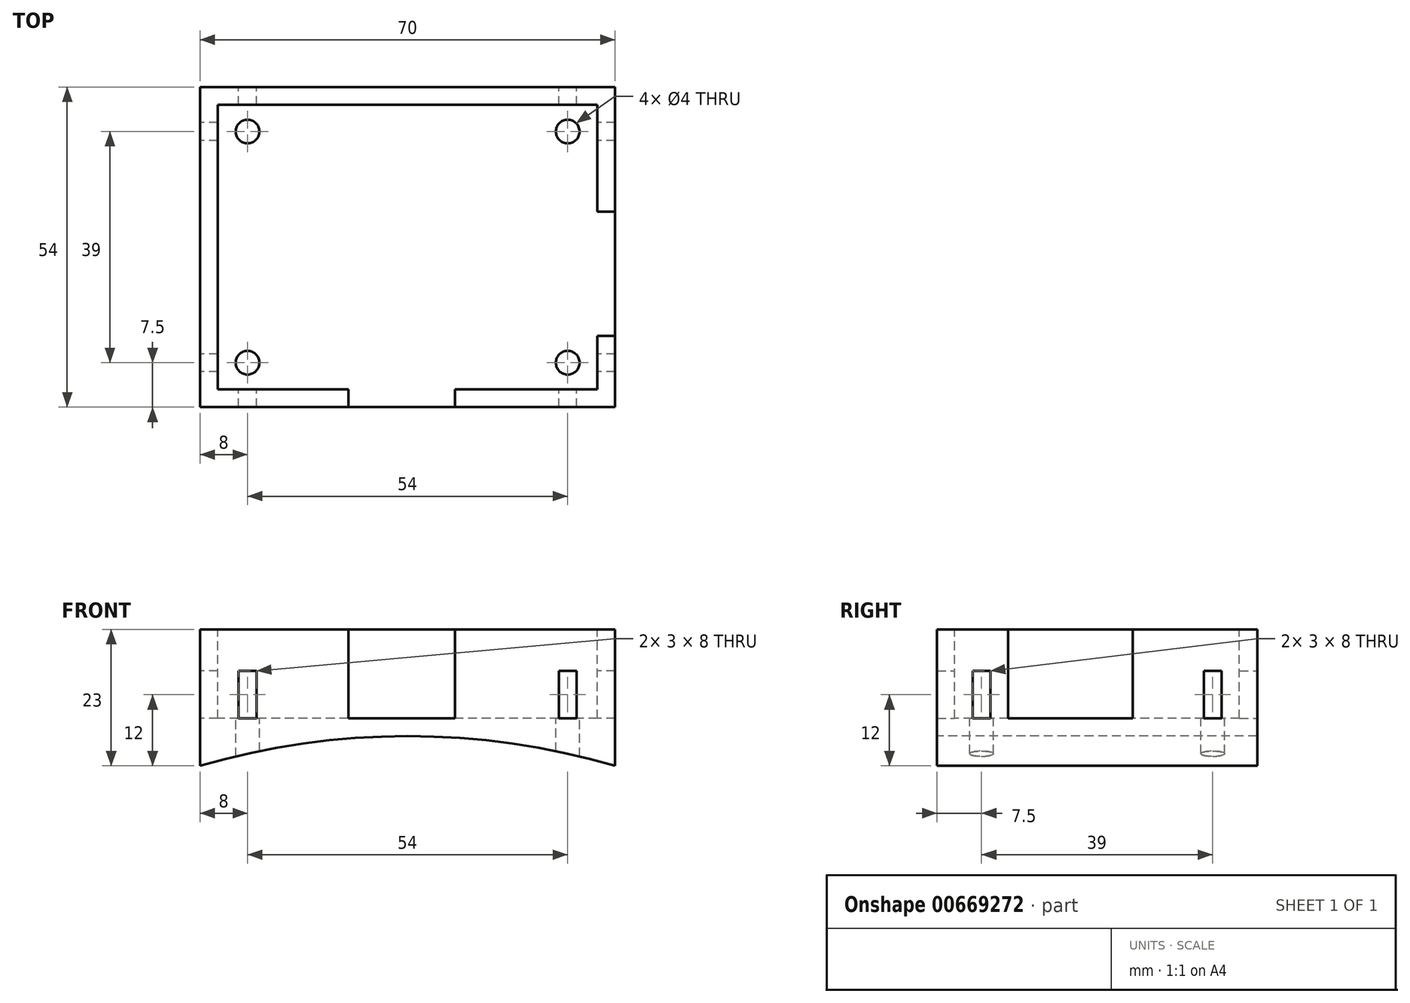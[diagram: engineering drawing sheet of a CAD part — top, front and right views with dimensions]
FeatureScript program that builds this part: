
annotation { "Feature Type Name" : "Feature", "Feature Type Description" : "" }
export const myFeature = defineFeature(function(context is Context, id is Id, definition is map)
    precondition{}
    {
        {
            var Q0;
            Q0=qCreatedBy(makeId("Top.planeOp"),FACE);
            var sketch = newSketch(context, id + "F0", { "sketchPlane" : qUnion([Q0])});
            skLineSegment(sketch, "E0.bottom", {"start": v(35, -27) * mm, "end": v(-35, -27) * mm});
            skLineSegment(sketch, "E0.top", {"start": v(35, 27) * mm, "end": v(-35, 27) * mm});
            skLineSegment(sketch, "E0.left", {"start": v(35, -27) * mm, "end": v(35, 27) * mm});
            skLineSegment(sketch, "E0.right", {"start": v(-35, -27) * mm, "end": v(-35, 27) * mm});
            skPoint(sketch, "E0.middle", {"position": v(0, 0) * mm});
            skSolve(sketch);
        }
        {
            var Q0;
            Q0=makeQuery(id+"F0.imprint","IMPRINT",FACE,{"disambiguationData":[TD([[makeQuery(id+"F0.imprint","IMPRINT",EDGE,{"derivedFrom":sQuery(id+"F0.wireOp",EDGE,"E0.bottom")}),-1.0]])]});
            extrude(context, id + "F1", {"entities" : qUnion([Q0]), "oppositeDirection" : true, "depth" : 23 * mm, "offsetDistance" : 25 * mm});
        }
        {
            var Q0;
            Q0=makeQuery(id+"F1.opExtrude","SWEPT_FACE",FACE,{"disambiguationData":[OSD([sQuery(id+"F0.wireOp",EDGE,"E0.bottom")])]});
            var sketch = newSketch(context, id + "F2", { "sketchPlane" : qUnion([Q0])});
            skArc(sketch, "E1", {"start": v(35, -23) * mm, "mid": v(0, -18) * mm, "end": v(-35, -23) * mm});
            skSolve(sketch);
        }
        {
            var Q0;
            Q0=makeQuery(id+"F2.imprint","IMPRINT",FACE,{"disambiguationData":[TD([[makeQuery(id+"F2.imprint","IMPRINT",EDGE,{"derivedFrom":sQuery(id+"F2.wireOp",EDGE,"E1")}),1.0]])]});
            extrude(context, id + "F3", {"entities" : qUnion([Q0]), "operationType" : NewBodyOperationType.REMOVE, "oppositeDirection" : true, "depth" : 60 * mm, "offsetDistance" : 25 * mm});
        }
        {
            var Q0;
            Q0=makeQuery(id+"F1.opExtrude","CAP_FACE",FACE,{"disambiguationData":[OSD([sQuery(id+"F0.wireOp",EDGE,"E0.bottom"),sQuery(id+"F0.wireOp",EDGE,"E0.top"),sQuery(id+"F0.wireOp",EDGE,"E0.left"),sQuery(id+"F0.wireOp",EDGE,"E0.right")])],"isStart":true});
            var sketch = newSketch(context, id + "F4", { "sketchPlane" : qUnion([Q0])});
            skLineSegment(sketch, "E2.bottom", {"start": v(32, 24) * mm, "end": v(-32, 24) * mm});
            skLineSegment(sketch, "E2.top", {"start": v(32, -24) * mm, "end": v(-32, -24) * mm});
            skLineSegment(sketch, "E2.left", {"start": v(32, 24) * mm, "end": v(32, -24) * mm});
            skLineSegment(sketch, "E2.right", {"start": v(-32, 24) * mm, "end": v(-32, -24) * mm});
            skPoint(sketch, "E2.middle", {"position": v(0, 0) * mm});
            skSolve(sketch);
        }
        {
            var Q0;
            Q0=makeQuery(id+"F4.imprint","IMPRINT",FACE,{"disambiguationData":[TD([[makeQuery(id+"F4.imprint","IMPRINT",EDGE,{"derivedFrom":sQuery(id+"F4.wireOp",EDGE,"E2.bottom")}),1.0]])]});
            extrude(context, id + "F5", {"entities" : qUnion([Q0]), "operationType" : NewBodyOperationType.REMOVE, "oppositeDirection" : true, "depth" : 15 * mm, "offsetDistance" : 25 * mm});
        }
        {
            var Q0;
            Q0=makeQuery(id+"F5.boolean.opBoolean","COPY",FACE,{"derivedFrom":makeQuery(id+"F5.opExtrude","CAP_FACE",FACE,{"disambiguationData":[OSD([sQuery(id+"F4.wireOp",EDGE,"E2.bottom"),sQuery(id+"F4.wireOp",EDGE,"E2.top"),sQuery(id+"F4.wireOp",EDGE,"E2.left"),sQuery(id+"F4.wireOp",EDGE,"E2.right")])],"isStart":false})});
            var sketch = newSketch(context, id + "F6", { "sketchPlane" : qUnion([Q0])});
            skPoint(sketch, "E3.middle", {"position": v(0, 0) * mm});
            skCircle(sketch, "E4", {"center": v(-27, 19.5) * mm, "radius": 2 * mm});
            skCircle(sketch, "E5", {"center": v(-27, -19.5) * mm, "radius": 2 * mm});
            skCircle(sketch, "E6", {"center": v(27, -19.5) * mm, "radius": 2 * mm});
            skCircle(sketch, "E7", {"center": v(27, 19.5) * mm, "radius": 2 * mm});
            skSolve(sketch);
        }
        {
            var Q0;
            Q0 = qSketchRegion(id + "F6", true);
            extrude(context, id + "F7", {"entities" : qUnion([Q0]), "operationType" : NewBodyOperationType.REMOVE, "oppositeDirection" : true, "depth" : 25 * mm, "offsetDistance" : 25 * mm});
        }
        {
            var Q0;
            Q0=makeQuery(id+"F5.boolean.opBoolean","COPY",FACE,{"derivedFrom":makeQuery(id+"F5.opExtrude","CAP_FACE",FACE,{"disambiguationData":[OSD([sQuery(id+"F4.wireOp",EDGE,"E2.bottom"),sQuery(id+"F4.wireOp",EDGE,"E2.top"),sQuery(id+"F4.wireOp",EDGE,"E2.left"),sQuery(id+"F4.wireOp",EDGE,"E2.right")])],"isStart":false})});
            var sketch = newSketch(context, id + "F8", { "sketchPlane" : qUnion([Q0])});
            skLineSegment(sketch, "E8.top", {"start": v(32, 6) * mm, "end": v(37, 6) * mm});
            skLineSegment(sketch, "E9.top", {"start": v(32, -15) * mm, "end": v(38.88, -15) * mm});
            skLineSegment(sketch, "E10.bottom", {"start": v(32, 6) * mm, "end": v(32, 6) * mm});
            skLineSegment(sketch, "E10.top", {"start": v(32, -15) * mm, "end": v(32, -15) * mm});
            skLineSegment(sketch, "E10.left", {"start": v(32, 6) * mm, "end": v(32, -15) * mm});
            skLineSegment(sketch, "E10.right", {"start": v(32, 6) * mm, "end": v(32, -15) * mm});
            skLineSegment(sketch, "E11.bottom", {"start": v(32, 6) * mm, "end": v(38.88, 6) * mm});
            skLineSegment(sketch, "E11.right", {"start": v(38.88, 6) * mm, "end": v(38.88, -15) * mm});
            skSolve(sketch);
        }
        {
            var Q0;
            Q0 = qSketchRegion(id + "F8", true);
            extrude(context, id + "F9", {"entities" : qUnion([Q0]), "operationType" : NewBodyOperationType.REMOVE, "depth" : 25 * mm, "offsetDistance" : 25 * mm});
        }
        {
            var Q0;
            Q0=makeQuery(id+"F9.boolean.opBoolean","MERGE",FACE,{"derivedFrom":[makeQuery(id+"F5.boolean.opBoolean","COPY",FACE,{"derivedFrom":makeQuery(id+"F5.opExtrude","CAP_FACE",FACE,{"disambiguationData":[OSD([sQuery(id+"F4.wireOp",EDGE,"E2.bottom"),sQuery(id+"F4.wireOp",EDGE,"E2.top"),sQuery(id+"F4.wireOp",EDGE,"E2.left"),sQuery(id+"F4.wireOp",EDGE,"E2.right")])],"isStart":false})}),makeQuery(id+"F9.opExtrude","CAP_FACE",FACE,{"disambiguationData":[OSD([sQuery(id+"F8.wireOp",EDGE,"E11.bottom"),sQuery(id+"F8.wireOp",EDGE,"E9.top"),sQuery(id+"F8.wireOp",EDGE,"E10.left"),sQuery(id+"F8.wireOp",EDGE,"E11.right")])],"isStart":true})]});
            var sketch = newSketch(context, id + "F10", { "sketchPlane" : qUnion([Q0])});
            skLineSegment(sketch, "E12.right", {"start": v(-10, -24) * mm, "end": v(-10, -27.84) * mm});
            skLineSegment(sketch, "E13.bottom", {"start": v(8, -24) * mm, "end": v(-10, -24) * mm});
            skLineSegment(sketch, "E13.top", {"start": v(8, -32.82) * mm, "end": v(-10, -32.82) * mm});
            skLineSegment(sketch, "E13.left", {"start": v(8, -24) * mm, "end": v(8, -32.82) * mm});
            skLineSegment(sketch, "E13.right", {"start": v(-10, -24) * mm, "end": v(-10, -32.82) * mm});
            skSolve(sketch);
        }
        {
            var Q0;
            Q0 = qSketchRegion(id + "F10", true);
            extrude(context, id + "F11", {"entities" : qUnion([Q0]), "operationType" : NewBodyOperationType.REMOVE, "depth" : 25 * mm, "offsetDistance" : 25 * mm});
        }
        {
            var Q0;
            Q0=makeQuery(id+"F11.boolean.opBoolean","MERGE",FACE,{"derivedFrom":[makeQuery(id+"F9.boolean.opBoolean","MERGE",FACE,{"derivedFrom":[makeQuery(id+"F5.boolean.opBoolean","COPY",FACE,{"derivedFrom":makeQuery(id+"F5.opExtrude","CAP_FACE",FACE,{"disambiguationData":[OSD([sQuery(id+"F4.wireOp",EDGE,"E2.bottom"),sQuery(id+"F4.wireOp",EDGE,"E2.top"),sQuery(id+"F4.wireOp",EDGE,"E2.left"),sQuery(id+"F4.wireOp",EDGE,"E2.right")])],"isStart":false})}),makeQuery(id+"F9.opExtrude","CAP_FACE",FACE,{"disambiguationData":[OSD([sQuery(id+"F8.wireOp",EDGE,"E11.bottom"),sQuery(id+"F8.wireOp",EDGE,"E9.top"),sQuery(id+"F8.wireOp",EDGE,"E10.left"),sQuery(id+"F8.wireOp",EDGE,"E11.right")])],"isStart":true})]}),makeQuery(id+"F11.opExtrude","CAP_FACE",FACE,{"disambiguationData":[OSD([sQuery(id+"F10.wireOp",EDGE,"E13.bottom"),sQuery(id+"F10.wireOp",EDGE,"E13.top"),sQuery(id+"F10.wireOp",EDGE,"E13.left"),sQuery(id+"F10.wireOp",EDGE,"E13.right")])],"isStart":true})]});
            var sketch = newSketch(context, id + "F12", { "sketchPlane" : qUnion([Q0])});
            skLineSegment(sketch, "E14", {"start": v(27, 19.5) * mm, "end": v(27, -19.5) * mm});
            skLineSegment(sketch, "E15", {"start": v(27, -19.5) * mm, "end": v(-27, -19.5) * mm});
            skLineSegment(sketch, "E16", {"start": v(-27, -19.5) * mm, "end": v(-27, 19.5) * mm});
            skLineSegment(sketch, "E17.bottom", {"start": v(-25.5, -31.14) * mm, "end": v(-28.5, -31.14) * mm});
            skLineSegment(sketch, "E17.top", {"start": v(-25.5, 70.14) * mm, "end": v(-28.5, 70.14) * mm});
            skLineSegment(sketch, "E17.left", {"start": v(-25.5, -31.14) * mm, "end": v(-25.5, 70.14) * mm});
            skLineSegment(sketch, "E17.right", {"start": v(-28.5, -31.14) * mm, "end": v(-28.5, 70.14) * mm});
            skPoint(sketch, "E17.middle", {"position": v(-27, 19.5) * mm});
            skLineSegment(sketch, "E18.bottom", {"start": v(28.5, -31.14) * mm, "end": v(25.5, -31.14) * mm});
            skLineSegment(sketch, "E18.top", {"start": v(28.5, 70.14) * mm, "end": v(25.5, 70.14) * mm});
            skLineSegment(sketch, "E18.left", {"start": v(28.5, -31.14) * mm, "end": v(28.5, 70.14) * mm});
            skLineSegment(sketch, "E18.right", {"start": v(25.5, -31.14) * mm, "end": v(25.5, 70.14) * mm});
            skPoint(sketch, "E18.middle", {"position": v(27, 19.5) * mm});
            skLineSegment(sketch, "E19.bottom", {"start": v(41.25, -21) * mm, "end": v(-95.25, -21) * mm});
            skLineSegment(sketch, "E19.top", {"start": v(41.25, -18) * mm, "end": v(-95.25, -18) * mm});
            skLineSegment(sketch, "E19.left", {"start": v(41.25, -21) * mm, "end": v(41.25, -18) * mm});
            skLineSegment(sketch, "E19.right", {"start": v(-95.25, -21) * mm, "end": v(-95.25, -18) * mm});
            skPoint(sketch, "E19.middle", {"position": v(-27, -19.5) * mm});
            skLineSegment(sketch, "E20.bottom", {"start": v(41.78, 18) * mm, "end": v(-95.78, 18) * mm});
            skLineSegment(sketch, "E20.top", {"start": v(41.78, 21) * mm, "end": v(-95.78, 21) * mm});
            skLineSegment(sketch, "E20.left", {"start": v(41.78, 18) * mm, "end": v(41.78, 21) * mm});
            skLineSegment(sketch, "E20.right", {"start": v(-95.78, 18) * mm, "end": v(-95.78, 21) * mm});
            skSolve(sketch);
        }
        {
            var Q0;
            Q0 = qSketchRegion(id + "F12", true);
            extrude(context, id + "F13", {"entities" : qUnion([Q0]), "operationType" : NewBodyOperationType.REMOVE, "depth" : 8 * mm, "offsetDistance" : 25 * mm});
        }
    });
